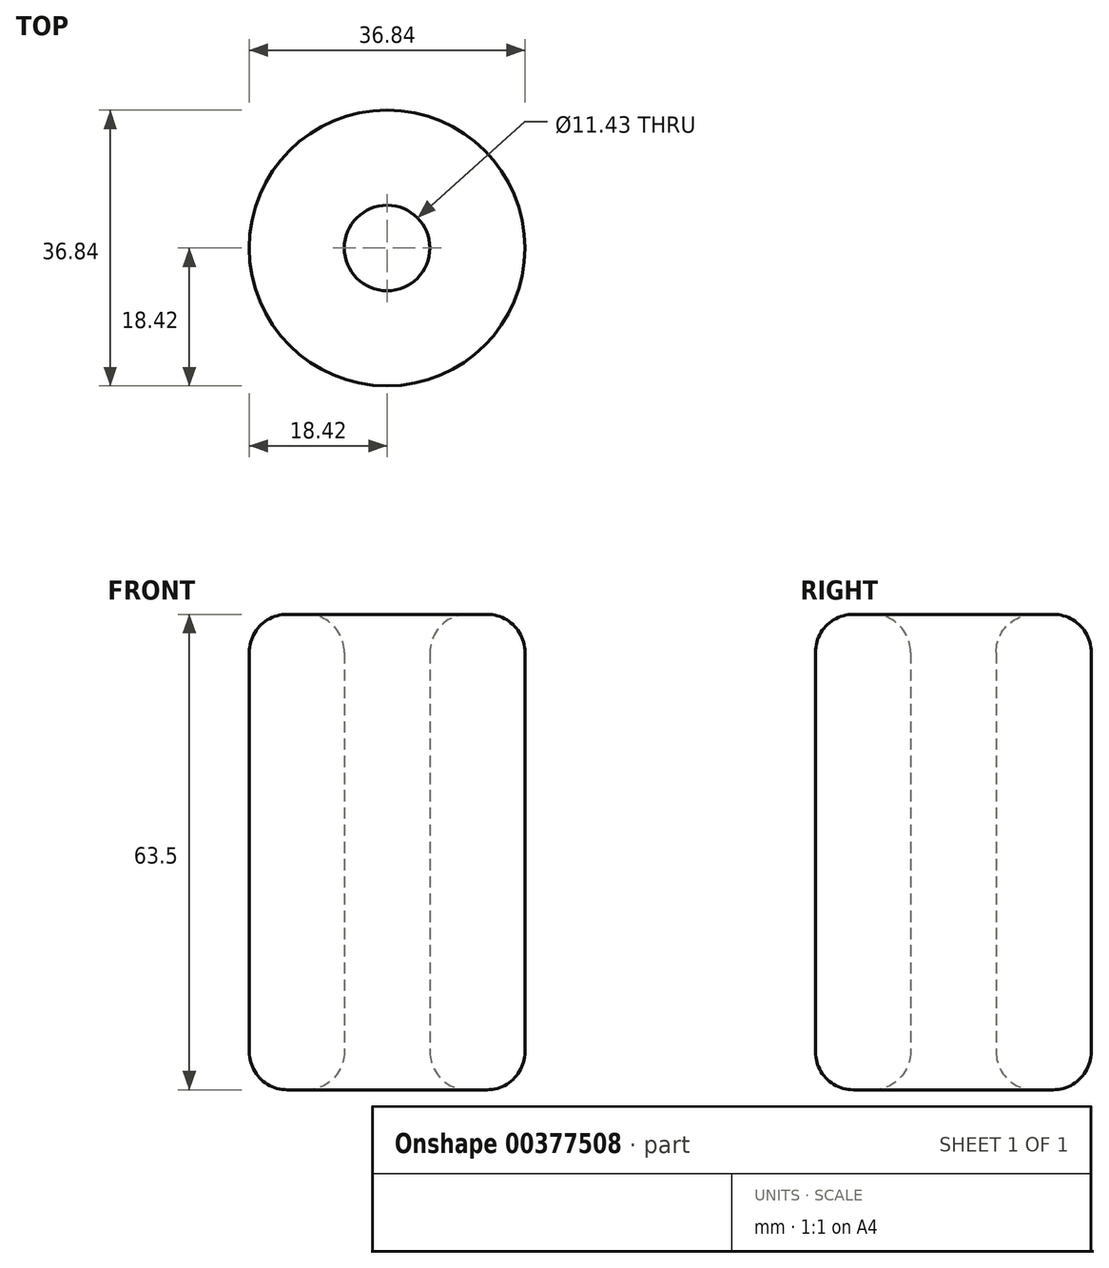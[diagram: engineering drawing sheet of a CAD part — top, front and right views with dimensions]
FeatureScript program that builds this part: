
annotation { "Feature Type Name" : "Feature", "Feature Type Description" : "" }
export const myFeature = defineFeature(function(context is Context, id is Id, definition is map)
    precondition{}
    {
        {
            var Q0;
            Q0=qCreatedBy(makeId("Top.planeOp"),FACE);
            var sketch = newSketch(context, id + "F0", { "sketchPlane" : qUnion([Q0])});
            skCircle(sketch, "E0", {"center": v(0, 0) * mm, "radius": 5.72 * mm});
            skCircle(sketch, "E1", {"center": v(0, 0) * mm, "radius": 18.41 * mm});
            skSolve(sketch);
        }
        {
            var Q0;
            Q0=makeQuery(id+"F0.imprint","IMPRINT",FACE,{"disambiguationData":[TD([[makeQuery(id+"F0.imprint","IMPRINT",EDGE,{"derivedFrom":sQuery(id+"F0.wireOp",EDGE,"E0")}),-1.0]])]});
            extrude(context, id + "F1", {"entities" : qUnion([Q0]), "depth" : 63.5 * mm});
        }
        {
            var Q0;
            Q0=makeQuery(id+"F1.opExtrude","CAP_EDGE",EDGE,{"disambiguationData":[OSD([sQuery(id+"F0.wireOp",EDGE,"E0")])],"isStart":false});
            var Q1;
            Q1=makeQuery(id+"F1.opExtrude","CAP_EDGE",EDGE,{"disambiguationData":[OSD([sQuery(id+"F0.wireOp",EDGE,"E1")])],"isStart":false});
            var Q2;
            Q2=makeQuery(id+"F1.opExtrude","CAP_FACE",FACE,{"disambiguationData":[OSD([sQuery(id+"F0.wireOp",EDGE,"E0"),sQuery(id+"F0.wireOp",EDGE,"E1")])],"isStart":true});
            fillet(context, id + "F2", {"entities" : qUnion([Q0, Q1, Q2]), "radius" : 5.08 * mm, "tangentPropagation" : true, "allowEdgeOverflow" : false});
        }
    });
